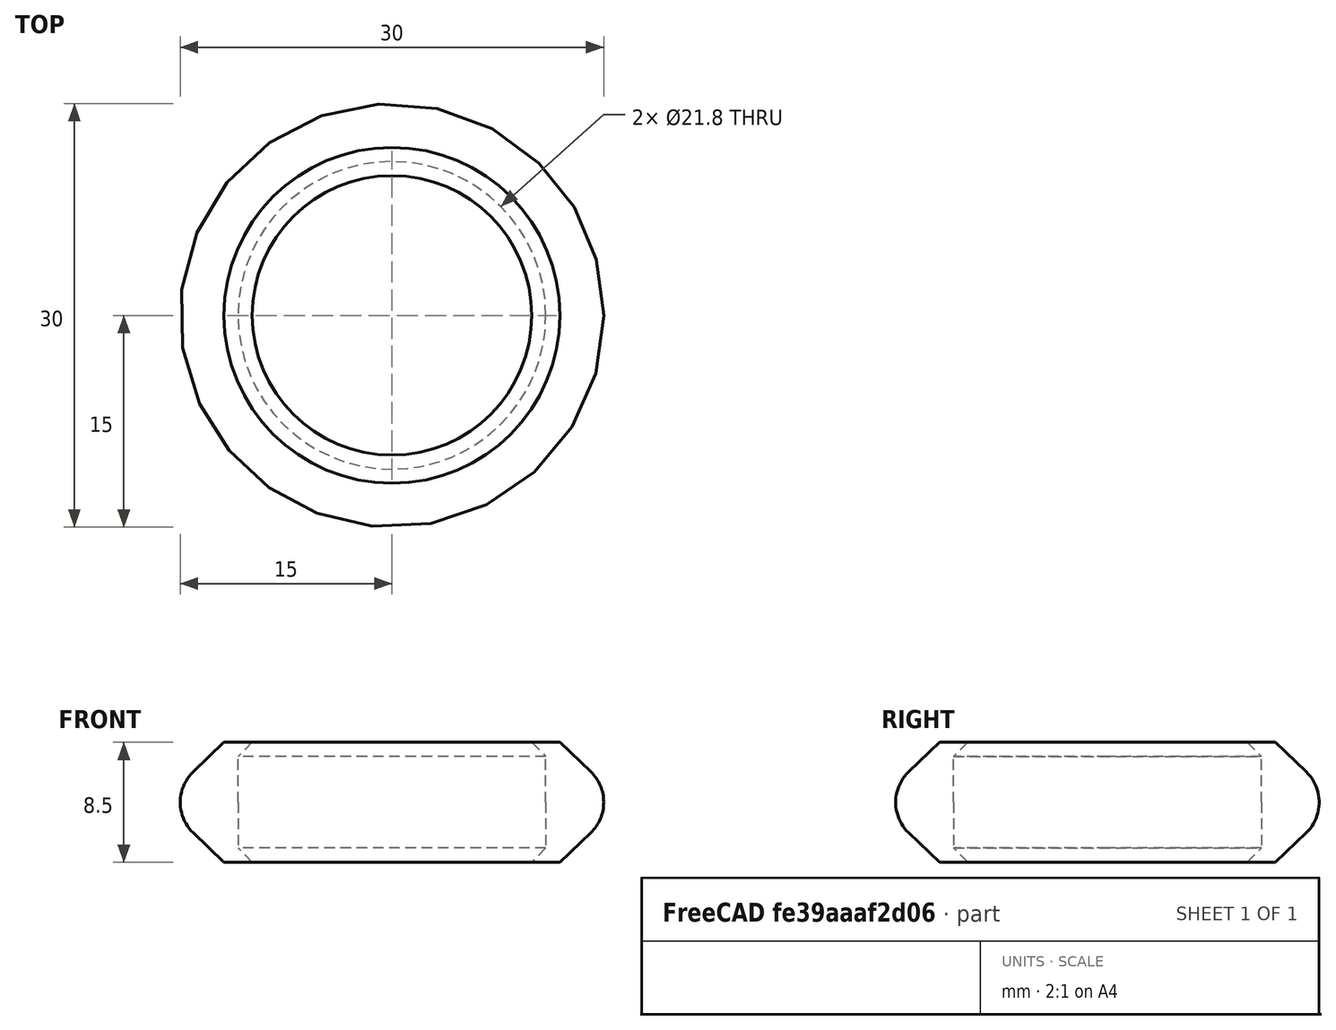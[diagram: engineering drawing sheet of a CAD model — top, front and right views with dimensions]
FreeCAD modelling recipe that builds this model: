
FCSTD DOCUMENT  (FreeCAD 0.20R29177 +426 (Git))
Label: TableRollerTire
License: All rights reserved
LicenseURL: http://en.wikipedia.org/wiki/All_rights_reserved
objects: App::DocumentObjectGroup×3, PartDesign::CoordinateSystem×1, App::FeaturePython×1, Sketcher::SketchObject×1, PartDesign::Revolution×1, PartDesign::Body×1, App::Part×1
note: 5 computed .brp shape members not serialized (recipe doc carries the construction recipe); baked Part::Feature solids carry a one-line shape summary decoded from their .brp

FEATURE [App::DocumentObjectGroup] Parts
FEATURE [PartDesign::CoordinateSystem] LCS_Origin
  AttacherType = Attacher::AttachEngine3D
  MapMode = 2
  Support = -> [X_Axis]
FEATURE [App::FeaturePython] Variables  # WARN: FeaturePython — macro-defined, semantics opaque (R4)
  Type = App::PropertyContainer
FEATURE [App::DocumentObjectGroup] Constraints
FEATURE [App::DocumentObjectGroup] Configurations
FEATURE [Sketcher::SketchObject] Sketch
  FullyConstrained = true
  MapMode = 5
  Placement = pos=(0,0,0) rot=(1,0,0;1.5708rad)
  Support = -> [XZ_Plane001]
  sketch-geometry (11):
    g0: LineSegment StartX=9.9 StartY=4.25 StartZ=0 EndX=9.9 EndY=-4.25 EndZ=0
    g1: ArcOfCircle CenterX=12 CenterY=0 CenterZ=0 NormalX=0 NormalY=0 NormalZ=1 AngleXU=0 Radius=3 StartAngle=5.47627 EndAngle=7.0901
    g2: LineSegment StartX=14.0752 StartY=2.16647 StartZ=0 EndX=11.9 EndY=4.25 EndZ=0
    g3: LineSegment StartX=14.0752 StartY=-2.16647 StartZ=0 EndX=11.9 EndY=-4.25 EndZ=0
    g4: LineSegment StartX=11.9 StartY=-4.25 StartZ=0 EndX=9.9 EndY=-4.25 EndZ=0
    g5: LineSegment StartX=11.9 StartY=4.25 StartZ=0 EndX=9.9 EndY=4.25 EndZ=0
    g6: GeomPoint X=15 Y=0 Z=0
    g7: LineSegment StartX=10.9 StartY=0 StartZ=0 EndX=10.9 EndY=3.25 EndZ=0
    g8: LineSegment StartX=10.9 StartY=0 StartZ=0 EndX=10.9 EndY=-3.25 EndZ=0
    g9: LineSegment StartX=9.9 StartY=4.25 StartZ=0 EndX=10.9 EndY=3.25 EndZ=0
    g10: LineSegment StartX=10.9 StartY=-3.25 StartZ=0 EndX=9.9 EndY=-4.25 EndZ=0
  constraints (30):
    c: Vertical(g0)
    c: PointOnObject(g1,g-1)
    c: Radius(g1) = 3
    c: DistanceY(g0,g0) = 8.5
    c: Tangent(g2,g1) = -1.5708
    c: Coincident(g4,g3)
    c: Horizontal(g4)
    c: Tangent(g3,g1) = 1.5708
    c: Coincident(g5,g2)
    c: Horizontal(g5)
    c: Coincident(g5,g0)
    c: Coincident(g4,g0)
    c: Equal(g4,g5)
    c: DistanceX(g5,g5) = 2
    c: PointOnObject(g6,g1)
    c: PointOnObject(g6,g-1)
    c: DistanceX(g-1,g6) = 15
    c: PointOnObject(g7,g-1)
    c: Vertical(g7)
    c: Coincident(g8,g7)
    c: Vertical(g8)
    c: Equal(g8,g7)
    c: DistanceY(g8,g7) = 6.5
    c: Coincident(g9,g5)
    c: Coincident(g9,g7)
    c: Coincident(g10,g8)
    c: Coincident(g10,g4)
    c: Equal(g10,g9)
    c: Angle(g9,g-1) = 0.785398
    c: DistanceX(g-1,g7) = 10.9
FEATURE [PartDesign::Revolution] Revolution
  Angle = 360
  Axis = (0,-2e-16,1)
  Base = (0,0,0)
  Placement = pos=(0,0,0) rot=(1,0,0;1.5708rad)
  Profile = -> Sketch
  ReferenceAxis = -> Sketch [V_Axis]
  Reversed = true
FEATURE [PartDesign::Body] Body
  Group = -> [Sketch,Revolution]
  Origin = -> Origin001
  Tip = -> Revolution
FEATURE [App::Part] Assembly
  AssemblyType = Part::Link
  Group = -> [LCS_Origin,Variables,Constraints,Configurations,Body]
  Origin = -> Origin
  Type = Assembly
